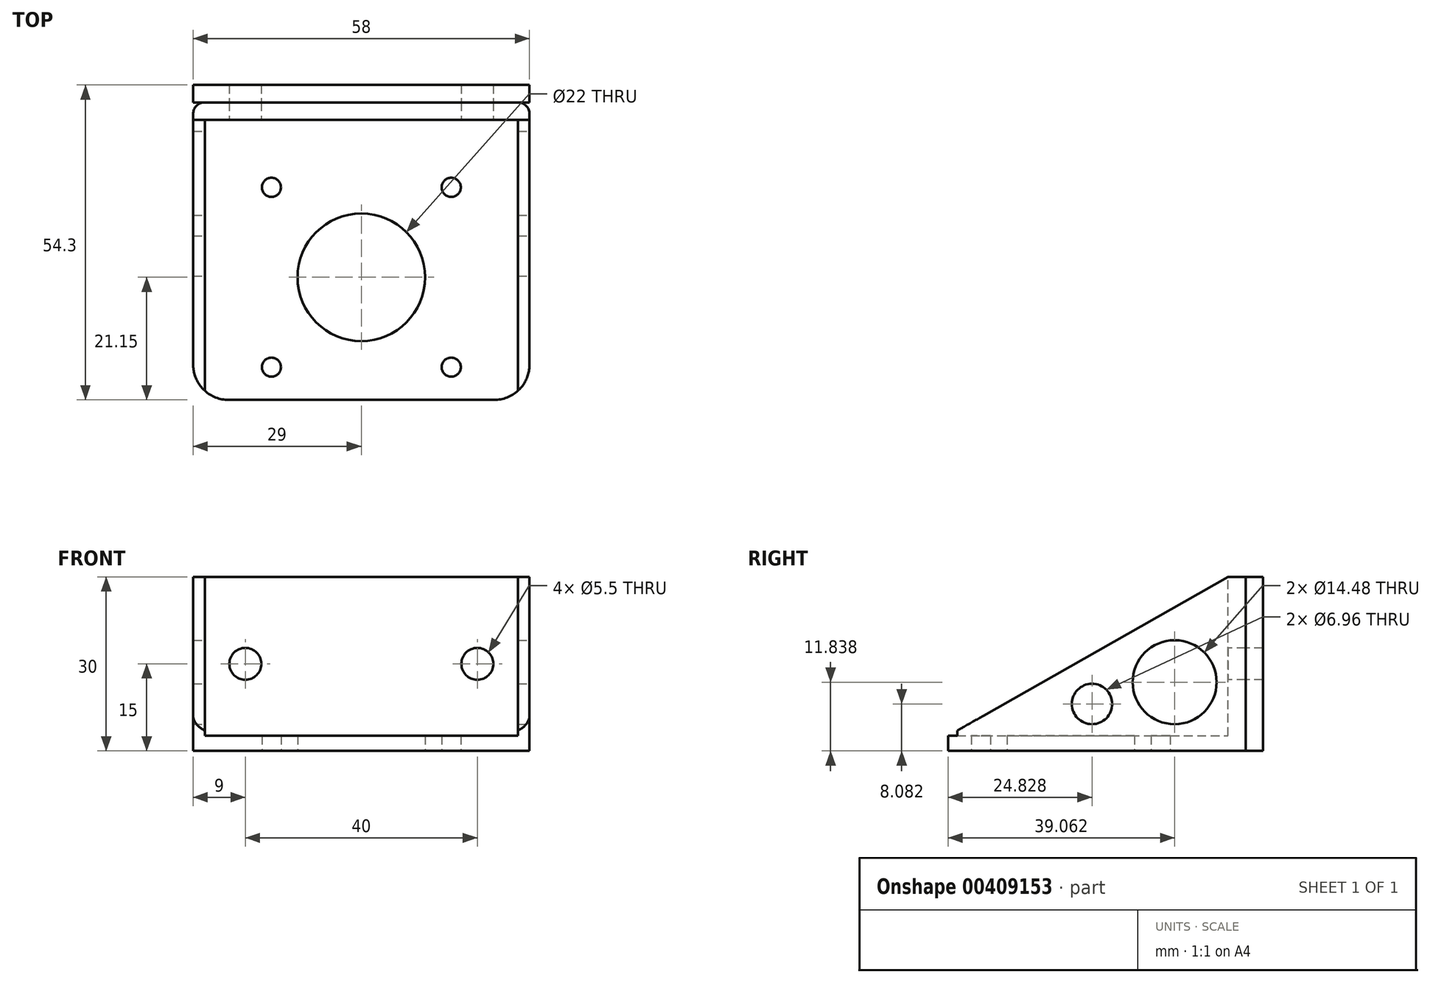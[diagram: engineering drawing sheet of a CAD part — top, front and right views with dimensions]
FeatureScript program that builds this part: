
annotation { "Feature Type Name" : "Feature", "Feature Type Description" : "" }
export const myFeature = defineFeature(function(context is Context, id is Id, definition is map)
    precondition{}
    {
        {
            var Q0;
            Q0=qCreatedBy(makeId("Top.planeOp"),FACE);
            var sketch = newSketch(context, id + "F0", { "sketchPlane" : qUnion([Q0])});
            skLineSegment(sketch, "E0.bottom", {"start": v(-21.15, 21.15) * mm, "end": v(21.15, 21.15) * mm, "construction": true});
            skLineSegment(sketch, "E0.top", {"start": v(-21.15, -21.15) * mm, "end": v(21.15, -21.15) * mm, "construction": true});
            skLineSegment(sketch, "E0.left", {"start": v(-21.15, 21.15) * mm, "end": v(-21.15, -21.15) * mm, "construction": true});
            skLineSegment(sketch, "E0.right", {"start": v(21.15, 21.15) * mm, "end": v(21.15, -21.15) * mm, "construction": true});
            skPoint(sketch, "E0.middle", {"position": v(0, 0) * mm});
            skLineSegment(sketch, "E1.bottom", {"start": v(15.5, -15.5) * mm, "end": v(-15.5, -15.5) * mm, "construction": true});
            skLineSegment(sketch, "E1.top", {"start": v(15.5, 15.5) * mm, "end": v(-15.5, 15.5) * mm, "construction": true});
            skLineSegment(sketch, "E1.left", {"start": v(15.5, -15.5) * mm, "end": v(15.5, 15.5) * mm, "construction": true});
            skLineSegment(sketch, "E1.right", {"start": v(-15.5, -15.5) * mm, "end": v(-15.5, 15.5) * mm, "construction": true});
            skCircle(sketch, "E2", {"center": v(-15.5, 15.5) * mm, "radius": 1.65 * mm});
            skCircle(sketch, "E3", {"center": v(15.5, 15.5) * mm, "radius": 1.65 * mm});
            skCircle(sketch, "E4", {"center": v(-15.5, -15.5) * mm, "radius": 1.65 * mm});
            skCircle(sketch, "E5", {"center": v(15.5, -15.5) * mm, "radius": 1.65 * mm});
            skCircle(sketch, "E6", {"center": v(0, 0) * mm, "radius": 11 * mm});
            skPoint(sketch, "E7.startSnap0", {"position": v(-21.15, 0) * mm});
            skLineSegment(sketch, "E8", {"start": v(0, 21.15) * mm, "end": v(0, -21.15) * mm, "construction": true});
            skLineSegment(sketch, "E9.bottom", {"start": v(29, -21.15) * mm, "end": v(-29, -21.15) * mm});
            skLineSegment(sketch, "E9.top", {"start": v(29, 27.15) * mm, "end": v(-29, 27.15) * mm});
            skLineSegment(sketch, "E9.left", {"start": v(29, -21.15) * mm, "end": v(29, 27.15) * mm});
            skLineSegment(sketch, "E9.right", {"start": v(-29, -21.15) * mm, "end": v(-29, 27.15) * mm});
            skPoint(sketch, "E9.middle", {"position": v(0, 3) * mm});
            skSolve(sketch);
        }
        {
            var Q0;
            Q0=makeQuery(id+"F0.imprint","IMPRINT",FACE,{"disambiguationData":[TD([[makeQuery(id+"F0.imprint","IMPRINT",EDGE,{"derivedFrom":sQuery(id+"F0.wireOp",EDGE,"E2")}),-1.0]])]});
            extrude(context, id + "F1", {"entities" : qUnion([Q0]), "depth" : 2.6 * mm, "offsetDistance" : 25 * mm});
        }
        {
            var Q0;
            Q0=makeQuery(id+"F1.opExtrude","SWEPT_FACE",FACE,{"disambiguationData":[OSD([sQuery(id+"F0.wireOp",EDGE,"E9.top")])]});
            var sketch = newSketch(context, id + "F2", { "sketchPlane" : qUnion([Q0])});
            skLineSegment(sketch, "E10.bottom", {"start": v(29, 0) * mm, "end": v(-29, 0) * mm});
            skLineSegment(sketch, "E10.top", {"start": v(29, 30) * mm, "end": v(-29, 30) * mm});
            skLineSegment(sketch, "E10.left", {"start": v(29, 0) * mm, "end": v(29, 30) * mm});
            skLineSegment(sketch, "E10.right", {"start": v(-29, 0) * mm, "end": v(-29, 30) * mm});
            skPoint(sketch, "E10.middle", {"position": v(0, 15) * mm});
            skCircle(sketch, "E11", {"center": v(20, 15) * mm, "radius": 2.75 * mm});
            skLineSegment(sketch, "E12", {"start": v(29, 15) * mm, "end": v(-29, 15) * mm, "construction": true});
            skCircle(sketch, "E13.MirrorC", {"center": v(-20, 15) * mm, "radius": 2.75 * mm});
            skCircle(sketch, "E14", {"center": v(0, 15) * mm, "radius": 2.75 * mm, "construction": true});
            skSolve(sketch);
        }
        {
            var Q0;
            {var subQ2=sQuery(id+"F2.wireOp",EDGE,"E10.top");Q0=makeQuery(id+"F2.imprint","IMPRINT",FACE,{"disambiguationData":[TD([[makeQuery(id+"F2.imprint","IMPRINT",EDGE,{"derivedFrom":subQ2}),1.0]])]});}
            var Q1;
            {var subQ0=sQuery(id+"F2.wireOp",EDGE,"E10.bottom");Q1=makeQuery(id+"F2.imprint","IMPRINT",FACE,{"disambiguationData":[TD([[makeQuery(id+"F2.imprint","IMPRINT",EDGE,{"derivedFrom":subQ0}),1.0]])]});}
            extrude(context, id + "F3", {"entities" : qUnion([Q0, Q1]), "operationType" : NewBodyOperationType.ADD, "depth" : 3 * mm, "offsetDistance" : 25 * mm});
        }
        {
            var Q0;
            Q0=makeQuery(id+"F3.opExtrude","CAP_FACE",FACE,{"disambiguationData":[OSD([sQuery(id+"F2.wireOp",EDGE,"E10.bottom"),sQuery(id+"F2.wireOp",EDGE,"E10.top"),sQuery(id+"F2.wireOp",EDGE,"E10.left"),sQuery(id+"F2.wireOp",EDGE,"E10.right"),sQuery(id+"F2.wireOp",EDGE,"E11"),sQuery(id+"F2.wireOp",EDGE,"E13.MirrorC")])],"isStart":false});
            extrude(context, id + "F4", {"entities" : qUnion([Q0]), "depth" : 3 * mm, "offsetDistance" : 25 * mm});
        }
        {
            var Q0;
            Q0=makeQuery(id+"F3.boolean.opBoolean","MERGE",FACE,{"derivedFrom":[makeQuery(id+"F1.opExtrude","SWEPT_FACE",FACE,{"disambiguationData":[OSD([sQuery(id+"F0.wireOp",EDGE,"E9.right")])]}),makeQuery(id+"F3.opExtrude","SWEPT_FACE",FACE,{"disambiguationData":[OSD([sQuery(id+"F2.wireOp",EDGE,"E10.left")])]})]});
            var sketch = newSketch(context, id + "F5", { "sketchPlane" : qUnion([Q0])});
            skLineSegment(sketch, "E15", {"start": v(-27.15, 30) * mm, "end": v(21.15, 2.6) * mm});
            skSolve(sketch);
        }
        {
            var Q0;
            Q0=makeQuery(id+"F5.imprint","IMPRINT",FACE,{"disambiguationData":[TD([[makeQuery(id+"F5.imprint","IMPRINT",EDGE,{"derivedFrom":sQuery(id+"F5.wireOp",EDGE,"E15")}),-1.0]])]});
            extrude(context, id + "F6", {"entities" : qUnion([Q0]), "operationType" : NewBodyOperationType.ADD, "oppositeDirection" : true, "depth" : 2 * mm, "offsetDistance" : 25 * mm});
        }
        {
            var Q0;
            Q0=makeQuery(id+"F3.boolean.opBoolean","MERGE",FACE,{"derivedFrom":[makeQuery(id+"F1.opExtrude","SWEPT_FACE",FACE,{"disambiguationData":[OSD([sQuery(id+"F0.wireOp",EDGE,"E9.left")])]}),makeQuery(id+"F3.opExtrude","SWEPT_FACE",FACE,{"disambiguationData":[OSD([sQuery(id+"F2.wireOp",EDGE,"E10.right")])]})]});
            var sketch = newSketch(context, id + "F7", { "sketchPlane" : qUnion([Q0])});
            skLineSegment(sketch, "E16", {"start": v(27.15, 30) * mm, "end": v(-21.15, 2.6) * mm});
            skSolve(sketch);
        }
        {
            var Q0;
            Q0=makeQuery(id+"F7.imprint","IMPRINT",FACE,{"disambiguationData":[TD([[makeQuery(id+"F7.imprint","IMPRINT",EDGE,{"derivedFrom":sQuery(id+"F7.wireOp",EDGE,"E16")}),1.0]])]});
            extrude(context, id + "F8", {"entities" : qUnion([Q0]), "operationType" : NewBodyOperationType.ADD, "oppositeDirection" : true, "depth" : 2 * mm, "offsetDistance" : 25 * mm});
        }
        {
            var Q0;
            Q0=makeQuery(id+"F3.opExtrude","CAP_FACE",FACE,{"disambiguationData":[OSD([sQuery(id+"F2.wireOp",EDGE,"E10.bottom"),sQuery(id+"F2.wireOp",EDGE,"E10.top"),sQuery(id+"F2.wireOp",EDGE,"E10.left"),sQuery(id+"F2.wireOp",EDGE,"E10.right"),sQuery(id+"F2.wireOp",EDGE,"E11"),sQuery(id+"F2.wireOp",EDGE,"E13.MirrorC"),sQuery(id+"F2.wireOp",EDGE,"E14")])],"isStart":true});
            var sketch = newSketch(context, id + "F9", { "sketchPlane" : qUnion([Q0])});
            skCircle(sketch, "E17", {"center": v(-20, 15) * mm, "radius": 6 * mm});
            skCircle(sketch, "E18", {"center": v(20, 15) * mm, "radius": 6 * mm});
            skSolve(sketch);
        }
        {
            var Q0;
            Q0=makeQuery(id+"F1.opExtrude","CAP_EDGE",EDGE,{"disambiguationData":[OSD([sQuery(id+"F0.wireOp",EDGE,"E9.top")])],"isStart":false});
            var Q1;
            Q1=makeQuery(id+"F1.opExtrude","SWEPT_EDGE",EDGE,{"disambiguationData":[OSD([sQuery(id+"F0.wireOp",EDGE,"E9.bottom"),sQuery(id+"F0.wireOp",EDGE,"E9.right")])]});
            var Q2;
            Q2=makeQuery(id+"F1.opExtrude","SWEPT_EDGE",EDGE,{"disambiguationData":[OSD([sQuery(id+"F0.wireOp",EDGE,"E9.bottom"),sQuery(id+"F0.wireOp",EDGE,"E9.left")])]});
            fillet(context, id + "F10", {"entities" : qUnion([Q0, Q1, Q2]), "radius" : 6.1 * mm, "tangentPropagation" : true, "allowEdgeOverflow" : false});
        }
        {
            var Q0;
            Q0=makeQuery(id+"F3.opExtrude","CAP_EDGE",EDGE,{"disambiguationData":[OSD([sQuery(id+"F2.wireOp",EDGE,"E10.right")])],"isStart":false});
            var Q1;
            Q1=makeQuery(id+"F3.opExtrude","CAP_EDGE",EDGE,{"disambiguationData":[OSD([sQuery(id+"F2.wireOp",EDGE,"E10.left")])],"isStart":false});
            var Q2;
            Q2=makeQuery(id+"F8.opExtrude","CAP_EDGE",EDGE,{"disambiguationData":[OSD([sQuery(id+"F2.wireOp",EDGE,"E10.right")])],"isStart":false});
            var Q3;
            Q3=makeQuery(id+"F6.opExtrude","CAP_EDGE",EDGE,{"disambiguationData":[OSD([sQuery(id+"F2.wireOp",EDGE,"E10.left")])],"isStart":false});
            fillet(context, id + "F11", {"entities" : qUnion([Q0, Q1, Q2, Q3]), "radius" : 2 * mm, "tangentPropagation" : true, "allowEdgeOverflow" : false});
        }
        {
            var Q0;
            {var subQ0=sQuery(id+"F2.wireOp",EDGE,"E10.right");var subQ1=sQuery(id+"F0.wireOp",EDGE,"E9.left");Q0=makeQuery(id+"F8.boolean.opBoolean","MERGE",FACE,{"derivedFrom":[makeQuery(id+"F3.boolean.opBoolean","MERGE",FACE,{"derivedFrom":[makeQuery(id+"F1.opExtrude","SWEPT_FACE",FACE,{"disambiguationData":[OSD([subQ1])]}),makeQuery(id+"F3.opExtrude","SWEPT_FACE",FACE,{"disambiguationData":[OSD([subQ0])]})]}),makeQuery(id+"F8.opExtrude","CAP_FACE",FACE,{"disambiguationData":[OSD([subQ1,subQ0,sQuery(id+"F7.wireOp",EDGE,"E16")])],"isStart":true})]});}
            var sketch = newSketch(context, id + "F12", { "sketchPlane" : qUnion([Q0])});
            skLineSegment(sketch, "E19", {"start": v(-9.52, 4.6) * mm, "end": v(27.15, 25.4) * mm, "construction": true});
            skCircle(sketch, "E20", {"center": v(17.91, 11.84) * mm, "radius": 7.24 * mm});
            skCircle(sketch, "E21", {"center": v(3.68, 8.08) * mm, "radius": 3.48 * mm});
            skSolve(sketch);
        }
        {
            var Q0;
            Q0=makeQuery(id+"F12.imprint","IMPRINT",FACE,{"disambiguationData":[TD([[makeQuery(id+"F12.imprint","IMPRINT",EDGE,{"derivedFrom":sQuery(id+"F12.wireOp",EDGE,"E21")}),1.0]])]});
            var Q1;
            Q1=makeQuery(id+"F12.imprint","IMPRINT",FACE,{"disambiguationData":[TD([[makeQuery(id+"F12.imprint","IMPRINT",EDGE,{"derivedFrom":sQuery(id+"F12.wireOp",EDGE,"E20")}),1.0]])]});
            extrude(context, id + "F13", {"entities" : qUnion([Q0, Q1]), "operationType" : NewBodyOperationType.REMOVE, "endBound" : BoundingType.THROUGH_ALL, "oppositeDirection" : true, "depth" : 25 * mm, "offsetDistance" : 25 * mm});
        }
        {
            var Q0;
            Q0=makeQuery(id+"F9.imprint","IMPRINT",FACE,{"disambiguationData":[TD([[makeQuery(id+"F9.imprint","IMPRINT",EDGE,{"derivedFrom":sQuery(id+"F9.wireOp",EDGE,"E17")}),1.0]])]});
            var Q1;
            Q1=makeQuery(id+"F9.imprint","IMPRINT",FACE,{"disambiguationData":[TD([[makeQuery(id+"F9.imprint","IMPRINT",EDGE,{"derivedFrom":sQuery(id+"F9.wireOp",EDGE,"E18")}),1.0]])]});
            extrude(context, id + "F14", {"entities" : qUnion([Q0, Q1]), "operationType" : NewBodyOperationType.REMOVE, "depth" : 25 * mm, "offsetDistance" : 25 * mm});
        }
    });
